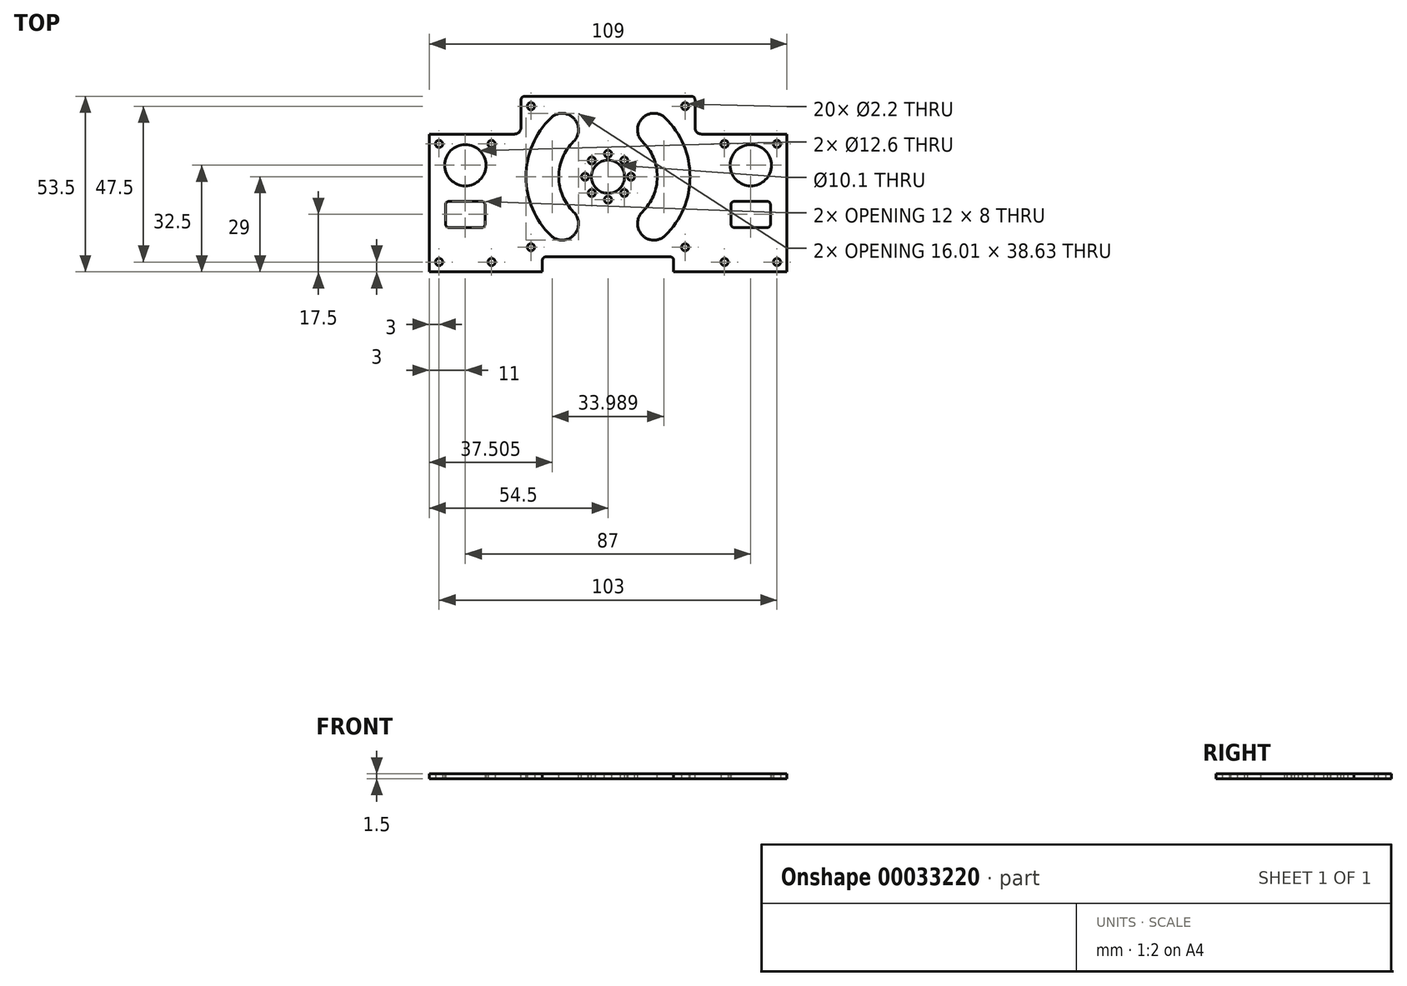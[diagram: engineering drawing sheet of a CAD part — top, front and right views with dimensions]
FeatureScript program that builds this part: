
annotation { "Feature Type Name" : "Feature", "Feature Type Description" : "" }
export const myFeature = defineFeature(function(context is Context, id is Id, definition is map)
    precondition{}
    {
        {
            var Q0;
            Q0=qCreatedBy(makeId("Top.planeOp"),FACE);
            var sketch = newSketch(context, id + "F0", { "sketchPlane" : qUnion([Q0])});
            skLineSegment(sketch, "E0.bottom", {"start": v(-54.5, 35) * mm, "end": v(54.5, 35) * mm});
            skLineSegment(sketch, "E0.top", {"start": v(-54.5, -35) * mm, "end": v(54.5, -35) * mm});
            skLineSegment(sketch, "E0.left", {"start": v(-54.5, 35) * mm, "end": v(-54.5, -35) * mm});
            skLineSegment(sketch, "E0.right", {"start": v(54.5, 35) * mm, "end": v(54.5, -35) * mm});
            skPoint(sketch, "E0.middle", {"position": v(0, 0) * mm});
            skLineSegment(sketch, "E1", {"start": v(-43.5, 35) * mm, "end": v(-43.5, -35) * mm, "construction": true});
            skCircle(sketch, "E2", {"center": v(-51.5, 10) * mm, "radius": 1.1 * mm});
            skCircle(sketch, "E3", {"center": v(-51.5, -26) * mm, "radius": 1.1 * mm});
            skCircle(sketch, "E4.MirrorC", {"center": v(-35.5, 10) * mm, "radius": 1.1 * mm});
            skCircle(sketch, "E5.MirrorC", {"center": v(-35.5, -26) * mm, "radius": 1.1 * mm});
            skCircle(sketch, "E6", {"center": v(-43.5, 3.5) * mm, "radius": 6.3 * mm});
            skCircle(sketch, "E7.MirrorC", {"center": v(35.5, -26) * mm, "radius": 1.1 * mm});
            skCircle(sketch, "E8.MirrorC", {"center": v(43.5, 3.5) * mm, "radius": 6.3 * mm});
            skCircle(sketch, "E9.MirrorC", {"center": v(35.5, 10) * mm, "radius": 1.1 * mm});
            skCircle(sketch, "E10.MirrorC", {"center": v(51.5, 10) * mm, "radius": 1.1 * mm});
            skCircle(sketch, "E11.MirrorC", {"center": v(51.5, -26) * mm, "radius": 1.1 * mm});
            skLineSegment(sketch, "E12.bottom", {"start": v(-38.5, -15.5) * mm, "end": v(-48.5, -15.5) * mm});
            skLineSegment(sketch, "E12.top", {"start": v(-38.5, -7.5) * mm, "end": v(-48.5, -7.5) * mm});
            skLineSegment(sketch, "E12.left", {"start": v(-37.5, -14.5) * mm, "end": v(-37.5, -8.5) * mm});
            skLineSegment(sketch, "E12.right", {"start": v(-49.5, -14.5) * mm, "end": v(-49.5, -8.5) * mm});
            skPoint(sketch, "E12.middle", {"position": v(-43.5, -11.5) * mm});
            skPoint(sketch, "E13.visualSharp", {"position": v(-49.5, -7.5) * mm});
            skArc(sketch, "E13.filletArc", {"start": v(-48.5, -7.5) * mm, "mid": v(-49.2, -7.8) * mm, "end": v(-49.5, -8.5) * mm});
            skPoint(sketch, "E14.visualSharp", {"position": v(-49.5, -15.5) * mm});
            skArc(sketch, "E14.filletArc", {"start": v(-49.5, -14.5) * mm, "mid": v(-49.2, -15.2) * mm, "end": v(-48.5, -15.5) * mm});
            skPoint(sketch, "E15.visualSharp", {"position": v(-37.5, -15.5) * mm});
            skArc(sketch, "E15.filletArc", {"start": v(-38.5, -15.5) * mm, "mid": v(-37.8, -15.2) * mm, "end": v(-37.5, -14.5) * mm});
            skPoint(sketch, "E16.visualSharp", {"position": v(-37.5, -7.5) * mm});
            skArc(sketch, "E16.filletArc", {"start": v(-37.5, -8.5) * mm, "mid": v(-37.8, -7.8) * mm, "end": v(-38.5, -7.5) * mm});
            skArc(sketch, "E17.MirrorCS", {"start": v(48.5, -7.5) * mm, "mid": v(49.2, -7.8) * mm, "end": v(49.5, -8.5) * mm});
            skArc(sketch, "E18.MirrorCS", {"start": v(38.5, -15.5) * mm, "mid": v(37.8, -15.2) * mm, "end": v(37.5, -14.5) * mm});
            skArc(sketch, "E19.MirrorCS", {"start": v(37.5, -8.5) * mm, "mid": v(37.8, -7.8) * mm, "end": v(38.5, -7.5) * mm});
            skArc(sketch, "E20.MirrorCS", {"start": v(49.5, -14.5) * mm, "mid": v(49.2, -15.2) * mm, "end": v(48.5, -15.5) * mm});
            skLineSegment(sketch, "E21.MirrorCS", {"start": v(49.5, -14.5) * mm, "end": v(49.5, -8.5) * mm});
            skLineSegment(sketch, "E22.MirrorCS", {"start": v(38.5, -15.5) * mm, "end": v(48.5, -15.5) * mm});
            skPoint(sketch, "E23.MirrorP", {"position": v(37.5, -15.5) * mm});
            skPoint(sketch, "E24.MirrorP", {"position": v(49.5, -15.5) * mm});
            skPoint(sketch, "E25.MirrorP", {"position": v(49.5, -7.5) * mm});
            skPoint(sketch, "E26.MirrorP", {"position": v(43.5, -11.5) * mm});
            skLineSegment(sketch, "E27.MirrorCS", {"start": v(38.5, -7.5) * mm, "end": v(48.5, -7.5) * mm});
            skLineSegment(sketch, "E28.MirrorCS", {"start": v(37.5, -14.5) * mm, "end": v(37.5, -8.5) * mm});
            skPoint(sketch, "E29.MirrorP", {"position": v(37.5, -7.5) * mm});
            skLineSegment(sketch, "E30", {"start": v(-32.5, 35) * mm, "end": v(-32.5, -35) * mm, "construction": true});
            skArc(sketch, "E31.MirrorCS", {"start": v(-27.5, -8.5) * mm, "mid": v(-27.2, -7.8) * mm, "end": v(-26.5, -7.5) * mm, "construction": true});
            skArc(sketch, "E32.MirrorCS", {"start": v(-15.5, -14.5) * mm, "mid": v(-15.8, -15.2) * mm, "end": v(-16.5, -15.5) * mm, "construction": true});
            skArc(sketch, "E33.MirrorCS", {"start": v(-26.5, -15.5) * mm, "mid": v(-27.2, -15.2) * mm, "end": v(-27.5, -14.5) * mm, "construction": true});
            skArc(sketch, "E34.MirrorCS", {"start": v(-16.5, -7.5) * mm, "mid": v(-15.8, -7.8) * mm, "end": v(-15.5, -8.5) * mm, "construction": true});
            skCircle(sketch, "E35.MirrorC", {"center": v(-13.5, -26) * mm, "radius": 1.1 * mm, "construction": true});
            skCircle(sketch, "E36.MirrorC", {"center": v(-29.5, 10) * mm, "radius": 1.1 * mm, "construction": true});
            skCircle(sketch, "E37.MirrorC", {"center": v(-29.5, -26) * mm, "radius": 1.1 * mm, "construction": true});
            skLineSegment(sketch, "E38.MirrorCS", {"start": v(-15.5, -14.5) * mm, "end": v(-15.5, -8.5) * mm, "construction": true});
            skCircle(sketch, "E39.MirrorC", {"center": v(-21.5, 3.5) * mm, "radius": 6.3 * mm, "construction": true});
            skLineSegment(sketch, "E40.MirrorCS", {"start": v(-26.5, -7.5) * mm, "end": v(-16.5, -7.5) * mm, "construction": true});
            skPoint(sketch, "E41.MirrorP", {"position": v(-21.5, -11.5) * mm});
            skLineSegment(sketch, "E42.MirrorCS", {"start": v(-27.5, -14.5) * mm, "end": v(-27.5, -8.5) * mm, "construction": true});
            skPoint(sketch, "E43.MirrorP", {"position": v(-15.5, -15.5) * mm});
            skPoint(sketch, "E44.MirrorP", {"position": v(-15.5, -7.5) * mm});
            skLineSegment(sketch, "E45.MirrorCS", {"start": v(-26.5, -15.5) * mm, "end": v(-16.5, -15.5) * mm, "construction": true});
            skPoint(sketch, "E46.MirrorP", {"position": v(-27.5, -15.5) * mm});
            skPoint(sketch, "E47.MirrorP", {"position": v(-27.5, -7.5) * mm});
            skCircle(sketch, "E48.MirrorC", {"center": v(-13.5, 10) * mm, "radius": 1.1 * mm, "construction": true});
            skArc(sketch, "E49.MirrorCS", {"start": v(15.5, -14.5) * mm, "mid": v(15.8, -15.2) * mm, "end": v(16.5, -15.5) * mm, "construction": true});
            skArc(sketch, "E50.MirrorCS", {"start": v(26.5, -15.5) * mm, "mid": v(27.2, -15.2) * mm, "end": v(27.5, -14.5) * mm, "construction": true});
            skArc(sketch, "E51.MirrorCS", {"start": v(16.5, -7.5) * mm, "mid": v(15.8, -7.8) * mm, "end": v(15.5, -8.5) * mm, "construction": true});
            skArc(sketch, "E52.MirrorCS", {"start": v(27.5, -8.5) * mm, "mid": v(27.2, -7.8) * mm, "end": v(26.5, -7.5) * mm, "construction": true});
            skLineSegment(sketch, "E53.MirrorCS", {"start": v(15.5, -14.5) * mm, "end": v(15.5, -8.5) * mm, "construction": true});
            skLineSegment(sketch, "E54.MirrorCS", {"start": v(26.5, -15.5) * mm, "end": v(16.5, -15.5) * mm, "construction": true});
            skLineSegment(sketch, "E55.MirrorCS", {"start": v(27.5, -14.5) * mm, "end": v(27.5, -8.5) * mm, "construction": true});
            skPoint(sketch, "E56.MirrorP", {"position": v(15.5, -15.5) * mm});
            skPoint(sketch, "E57.MirrorP", {"position": v(15.5, -7.5) * mm});
            skCircle(sketch, "E58.MirrorC", {"center": v(13.5, -26) * mm, "radius": 1.1 * mm, "construction": true});
            skPoint(sketch, "E59.MirrorP", {"position": v(27.5, -7.5) * mm});
            skCircle(sketch, "E60.MirrorC", {"center": v(13.5, 10) * mm, "radius": 1.1 * mm, "construction": true});
            skLineSegment(sketch, "E61.MirrorCS", {"start": v(26.5, -7.5) * mm, "end": v(16.5, -7.5) * mm, "construction": true});
            skPoint(sketch, "E62.MirrorP", {"position": v(27.5, -15.5) * mm});
            skPoint(sketch, "E63.MirrorP", {"position": v(21.5, -11.5) * mm});
            skCircle(sketch, "E64.MirrorC", {"center": v(21.5, 3.5) * mm, "radius": 6.3 * mm, "construction": true});
            skCircle(sketch, "E65.MirrorC", {"center": v(29.5, 10) * mm, "radius": 1.1 * mm, "construction": true});
            skCircle(sketch, "E66", {"center": v(-23.5, 21.5) * mm, "radius": 1.1 * mm});
            skCircle(sketch, "E67.MirrorC", {"center": v(23.5, 21.5) * mm, "radius": 1.1 * mm});
            skCircle(sketch, "E68.MirrorC", {"center": v(-23.5, -21.5) * mm, "radius": 1.1 * mm});
            skCircle(sketch, "E69.MirrorC", {"center": v(23.5, -21.5) * mm, "radius": 1.1 * mm});
            skSolve(sketch);
        }
        {
            var Q0;
            Q0=qSketchRegion(id+"F0",true);
            extrude(context, id + "F1", {"entities" : qUnion([Q0]), "depth" : 1.5 * mm});
        }
        {
            var Q0;
            Q0=makeQuery(id+"F1.opExtrude","CAP_FACE",FACE,{"disambiguationData":[OSD([sQuery(id+"F0.wireOp",EDGE,"E0.bottom"),sQuery(id+"F0.wireOp",EDGE,"E0.top"),sQuery(id+"F0.wireOp",EDGE,"E0.left"),sQuery(id+"F0.wireOp",EDGE,"E0.right"),sQuery(id+"F0.wireOp",EDGE,"E2"),sQuery(id+"F0.wireOp",EDGE,"E3"),sQuery(id+"F0.wireOp",EDGE,"E4.MirrorC"),sQuery(id+"F0.wireOp",EDGE,"E5.MirrorC"),sQuery(id+"F0.wireOp",EDGE,"E6"),sQuery(id+"F0.wireOp",EDGE,"E7.MirrorC"),sQuery(id+"F0.wireOp",EDGE,"E8.MirrorC"),sQuery(id+"F0.wireOp",EDGE,"E9.MirrorC"),sQuery(id+"F0.wireOp",EDGE,"E10.MirrorC"),sQuery(id+"F0.wireOp",EDGE,"E11.MirrorC"),sQuery(id+"F0.wireOp",EDGE,"E12.bottom"),sQuery(id+"F0.wireOp",EDGE,"E12.top"),sQuery(id+"F0.wireOp",EDGE,"E12.left"),sQuery(id+"F0.wireOp",EDGE,"E12.right"),sQuery(id+"F0.wireOp",EDGE,"E13.filletArc"),sQuery(id+"F0.wireOp",EDGE,"E14.filletArc"),sQuery(id+"F0.wireOp",EDGE,"E15.filletArc"),sQuery(id+"F0.wireOp",EDGE,"E16.filletArc"),sQuery(id+"F0.wireOp",EDGE,"E17.MirrorCS"),sQuery(id+"F0.wireOp",EDGE,"E18.MirrorCS"),sQuery(id+"F0.wireOp",EDGE,"E19.MirrorCS"),sQuery(id+"F0.wireOp",EDGE,"E20.MirrorCS"),sQuery(id+"F0.wireOp",EDGE,"E21.MirrorCS"),sQuery(id+"F0.wireOp",EDGE,"E22.MirrorCS"),sQuery(id+"F0.wireOp",EDGE,"E27.MirrorCS"),sQuery(id+"F0.wireOp",EDGE,"E28.MirrorCS"),sQuery(id+"F0.wireOp",EDGE,"E66"),sQuery(id+"F0.wireOp",EDGE,"E67.MirrorC"),sQuery(id+"F0.wireOp",EDGE,"E68.MirrorC"),sQuery(id+"F0.wireOp",EDGE,"E69.MirrorC")])],"isStart":false});
            var sketch = newSketch(context, id + "F2", { "sketchPlane" : qUnion([Q0])});
            skCircle(sketch, "E70", {"center": v(0, 0) * mm, "radius": 5.05 * mm});
            skCircle(sketch, "E71", {"center": v(0, 7) * mm, "radius": 1.1 * mm});
            skCircle(sketch, "E72.1.0", {"center": v(-4.95, 4.95) * mm, "radius": 1.1 * mm});
            skCircle(sketch, "E72.2.0", {"center": v(-7, 0) * mm, "radius": 1.1 * mm});
            skCircle(sketch, "E72.3.0", {"center": v(-4.95, -4.95) * mm, "radius": 1.1 * mm});
            skCircle(sketch, "E72.4.0", {"center": v(0, -7) * mm, "radius": 1.1 * mm});
            skCircle(sketch, "E72.5.0", {"center": v(4.95, -4.95) * mm, "radius": 1.1 * mm});
            skCircle(sketch, "E72.6.0", {"center": v(7, 0) * mm, "radius": 1.1 * mm});
            skCircle(sketch, "E72.7.0", {"center": v(4.95, 4.95) * mm, "radius": 1.1 * mm});
            skArc(sketch, "E73", {"start": v(-17.4, 17.95) * mm, "mid": v(-25, 0) * mm, "end": v(-17.4, -17.95) * mm});
            skArc(sketch, "E74", {"start": v(-10.47, 10.74) * mm, "mid": v(-15, 0) * mm, "end": v(-10.47, -10.74) * mm});
            skLineSegment(sketch, "E75", {"start": v(-9.75, 16.88) * mm, "end": v(-9.64, 16.7) * mm});
            skLineSegment(sketch, "E76.MirrorCS", {"start": v(-9.75, -16.88) * mm, "end": v(-9.64, -16.7) * mm});
            skLineSegment(sketch, "E77.MirrorCS", {"start": v(9.75, 16.88) * mm, "end": v(9.64, 16.7) * mm});
            skLineSegment(sketch, "E78.MirrorCS", {"start": v(9.75, -16.88) * mm, "end": v(9.64, -16.7) * mm});
            skArc(sketch, "E79.trimOffspring", {"start": v(10.47, -10.74) * mm, "mid": v(15, 0) * mm, "end": v(10.47, 10.74) * mm});
            skArc(sketch, "E80.trimOffspring", {"start": v(17.4, -17.95) * mm, "mid": v(25, 0) * mm, "end": v(17.4, 17.95) * mm});
            skPoint(sketch, "E81.visualSharp", {"position": v(-12.5, 21.65) * mm});
            skArc(sketch, "E81.filletArc", {"start": v(-9.75, 16.88) * mm, "mid": v(-13.31, 19.28) * mm, "end": v(-17.4, 17.95) * mm});
            skPoint(sketch, "E82.visualSharp", {"position": v(-7.5, 13) * mm});
            skArc(sketch, "E82.filletArc", {"start": v(-10.47, 10.74) * mm, "mid": v(-9.03, 13.58) * mm, "end": v(-9.64, 16.7) * mm});
            skPoint(sketch, "E83.visualSharp", {"position": v(-7.5, -13) * mm});
            skArc(sketch, "E83.filletArc", {"start": v(-9.64, -16.7) * mm, "mid": v(-9.03, -13.58) * mm, "end": v(-10.47, -10.74) * mm});
            skPoint(sketch, "E84.visualSharp", {"position": v(-12.5, -21.65) * mm});
            skArc(sketch, "E84.filletArc", {"start": v(-17.4, -17.95) * mm, "mid": v(-13.31, -19.28) * mm, "end": v(-9.75, -16.88) * mm});
            skPoint(sketch, "E85.visualSharp", {"position": v(7.5, -13) * mm});
            skArc(sketch, "E85.filletArc", {"start": v(10.47, -10.74) * mm, "mid": v(9.03, -13.58) * mm, "end": v(9.64, -16.7) * mm});
            skPoint(sketch, "E86.visualSharp", {"position": v(12.5, -21.65) * mm});
            skArc(sketch, "E86.filletArc", {"start": v(9.75, -16.88) * mm, "mid": v(13.31, -19.28) * mm, "end": v(17.4, -17.95) * mm});
            skPoint(sketch, "E87.visualSharp", {"position": v(7.5, 13) * mm});
            skArc(sketch, "E87.filletArc", {"start": v(9.64, 16.7) * mm, "mid": v(9.03, 13.58) * mm, "end": v(10.47, 10.74) * mm});
            skPoint(sketch, "E88.visualSharp", {"position": v(12.5, 21.65) * mm});
            skArc(sketch, "E88.filletArc", {"start": v(17.4, 17.95) * mm, "mid": v(13.31, 19.28) * mm, "end": v(9.75, 16.88) * mm});
            skLineSegment(sketch, "E89.bottom", {"start": v(-54.5, 35) * mm, "end": v(-26.5, 35) * mm});
            skLineSegment(sketch, "E89.top", {"start": v(-54.5, 13) * mm, "end": v(-28.5, 13) * mm});
            skLineSegment(sketch, "E89.left", {"start": v(-54.5, 35) * mm, "end": v(-54.5, 13) * mm});
            skLineSegment(sketch, "E89.right", {"start": v(-26.5, 35) * mm, "end": v(-26.5, 15) * mm});
            skPoint(sketch, "E90", {"position": v(-23.5, 21.5) * mm});
            skPoint(sketch, "E91", {"position": v(-35.5, 10) * mm});
            skLineSegment(sketch, "E92.MirrorCS", {"start": v(54.5, 13) * mm, "end": v(28.5, 13) * mm});
            skLineSegment(sketch, "E93.MirrorCS", {"start": v(54.5, 35) * mm, "end": v(26.5, 35) * mm});
            skPoint(sketch, "E94.MirrorP", {"position": v(23.5, 21.5) * mm});
            skLineSegment(sketch, "E95.MirrorCS", {"start": v(26.5, 35) * mm, "end": v(26.5, 15) * mm});
            skLineSegment(sketch, "E96.MirrorCS", {"start": v(54.5, 35) * mm, "end": v(54.5, 13) * mm});
            skPoint(sketch, "E97.MirrorP", {"position": v(35.5, 10) * mm});
            skPoint(sketch, "E98.visualSharp", {"position": v(-26.5, 13) * mm});
            skArc(sketch, "E98.filletArc", {"start": v(-28.5, 13) * mm, "mid": v(-27.09, 13.59) * mm, "end": v(-26.5, 15) * mm});
            skPoint(sketch, "E99.visualSharp", {"position": v(26.5, 13) * mm});
            skArc(sketch, "E99.filletArc", {"start": v(26.5, 15) * mm, "mid": v(27.09, 13.59) * mm, "end": v(28.5, 13) * mm});
            skLineSegment(sketch, "E100.bottom", {"start": v(-26.5, 35) * mm, "end": v(26.5, 35) * mm});
            skLineSegment(sketch, "E100.top", {"start": v(-26.5, 24.5) * mm, "end": v(26.5, 24.5) * mm});
            skLineSegment(sketch, "E100.left", {"start": v(-26.5, 35) * mm, "end": v(-26.5, 24.5) * mm});
            skLineSegment(sketch, "E100.right", {"start": v(26.5, 35) * mm, "end": v(26.5, 24.5) * mm});
            skLineSegment(sketch, "E101.bottom", {"start": v(20, -35) * mm, "end": v(-20, -35) * mm});
            skLineSegment(sketch, "E101.top", {"start": v(20, -24.43) * mm, "end": v(-20, -24.43) * mm});
            skLineSegment(sketch, "E101.left", {"start": v(20, -35) * mm, "end": v(20, -24.43) * mm});
            skLineSegment(sketch, "E101.right", {"start": v(-20, -35) * mm, "end": v(-20, -24.43) * mm});
            skPoint(sketch, "E101.middle", {"position": v(0, -29.72) * mm});
            skSolve(sketch);
        }
        {
            var Q0;
            Q0=qSketchRegion(id+"F2",true);
            extrude(context, id + "F3", {"entities" : qUnion([Q0]), "operationType" : NewBodyOperationType.REMOVE, "endBound" : BoundingType.UP_TO_NEXT, "oppositeDirection" : true, "depth" : 25 * mm});
        }
        {
            var Q0;
            Q0=makeQuery(id+"F1.opExtrude","CAP_FACE",FACE,{"disambiguationData":[OSD([sQuery(id+"F0.wireOp",EDGE,"E0.bottom"),sQuery(id+"F0.wireOp",EDGE,"E0.top"),sQuery(id+"F0.wireOp",EDGE,"E0.left"),sQuery(id+"F0.wireOp",EDGE,"E0.right"),sQuery(id+"F0.wireOp",EDGE,"E2"),sQuery(id+"F0.wireOp",EDGE,"E3"),sQuery(id+"F0.wireOp",EDGE,"E4.MirrorC"),sQuery(id+"F0.wireOp",EDGE,"E5.MirrorC"),sQuery(id+"F0.wireOp",EDGE,"E6"),sQuery(id+"F0.wireOp",EDGE,"E7.MirrorC"),sQuery(id+"F0.wireOp",EDGE,"E8.MirrorC"),sQuery(id+"F0.wireOp",EDGE,"E9.MirrorC"),sQuery(id+"F0.wireOp",EDGE,"E10.MirrorC"),sQuery(id+"F0.wireOp",EDGE,"E11.MirrorC"),sQuery(id+"F0.wireOp",EDGE,"E12.bottom"),sQuery(id+"F0.wireOp",EDGE,"E12.top"),sQuery(id+"F0.wireOp",EDGE,"E12.left"),sQuery(id+"F0.wireOp",EDGE,"E12.right"),sQuery(id+"F0.wireOp",EDGE,"E13.filletArc"),sQuery(id+"F0.wireOp",EDGE,"E14.filletArc"),sQuery(id+"F0.wireOp",EDGE,"E15.filletArc"),sQuery(id+"F0.wireOp",EDGE,"E16.filletArc"),sQuery(id+"F0.wireOp",EDGE,"E17.MirrorCS"),sQuery(id+"F0.wireOp",EDGE,"E18.MirrorCS"),sQuery(id+"F0.wireOp",EDGE,"E19.MirrorCS"),sQuery(id+"F0.wireOp",EDGE,"E20.MirrorCS"),sQuery(id+"F0.wireOp",EDGE,"E21.MirrorCS"),sQuery(id+"F0.wireOp",EDGE,"E22.MirrorCS"),sQuery(id+"F0.wireOp",EDGE,"E27.MirrorCS"),sQuery(id+"F0.wireOp",EDGE,"E28.MirrorCS"),sQuery(id+"F0.wireOp",EDGE,"E66"),sQuery(id+"F0.wireOp",EDGE,"E67.MirrorC"),sQuery(id+"F0.wireOp",EDGE,"E68.MirrorC"),sQuery(id+"F0.wireOp",EDGE,"E69.MirrorC")])],"isStart":false});
            var sketch = newSketch(context, id + "F4", { "sketchPlane" : qUnion([Q0])});
            skLineSegment(sketch, "E102.bottom", {"start": v(-54.5, -35) * mm, "end": v(-20, -35) * mm});
            skLineSegment(sketch, "E102.top", {"start": v(-54.5, -29) * mm, "end": v(-20, -29) * mm});
            skLineSegment(sketch, "E102.left", {"start": v(-54.5, -35) * mm, "end": v(-54.5, -29) * mm});
            skLineSegment(sketch, "E102.right", {"start": v(-20, -35) * mm, "end": v(-20, -29) * mm});
            skPoint(sketch, "E103", {"position": v(-51.5, -26) * mm});
            skLineSegment(sketch, "E104.MirrorCS", {"start": v(54.5, -35) * mm, "end": v(20, -35) * mm});
            skLineSegment(sketch, "E105.MirrorCS", {"start": v(54.5, -29) * mm, "end": v(20, -29) * mm});
            skLineSegment(sketch, "E106.MirrorCS", {"start": v(54.5, -35) * mm, "end": v(54.5, -29) * mm});
            skLineSegment(sketch, "E107.MirrorCS", {"start": v(20, -35) * mm, "end": v(20, -29) * mm});
            skSolve(sketch);
        }
        {
            var Q0;
            Q0 = qSketchRegion(id + "F4", true);
            extrude(context, id + "F5", {"entities" : qUnion([Q0]), "operationType" : NewBodyOperationType.REMOVE, "endBound" : BoundingType.UP_TO_NEXT, "oppositeDirection" : true, "depth" : 25 * mm});
        }
        {
            var Q0;
            Q0=makeQuery(id+"F5.boolean.opBoolean","COPY",EDGE,{"derivedFrom":makeQuery(id+"F5.opExtrude","SWEPT_EDGE",EDGE,{"disambiguationData":[OSD([sQuery(id+"F0.wireOp",EDGE,"E0.left"),sQuery(id+"F4.wireOp",EDGE,"E102.top"),sQuery(id+"F4.wireOp",EDGE,"E102.left")])]})});
            var Q1;
            Q1=makeQuery(id+"F5.boolean.opBoolean","COPY",EDGE,{"derivedFrom":makeQuery(id+"F5.opExtrude","SWEPT_EDGE",EDGE,{"disambiguationData":[OSD([sQuery(id+"F2.wireOp",EDGE,"E101.right"),sQuery(id+"F4.wireOp",EDGE,"E102.top"),sQuery(id+"F4.wireOp",EDGE,"E102.right")])]})});
            var Q2;
            Q2=makeQuery(id+"F5.boolean.opBoolean","COPY",EDGE,{"derivedFrom":makeQuery(id+"F5.opExtrude","SWEPT_EDGE",EDGE,{"disambiguationData":[OSD([sQuery(id+"F2.wireOp",EDGE,"E101.left"),sQuery(id+"F4.wireOp",EDGE,"E105.MirrorCS"),sQuery(id+"F4.wireOp",EDGE,"E107.MirrorCS")])]})});
            var Q3;
            Q3=makeQuery(id+"F5.boolean.opBoolean","COPY",EDGE,{"derivedFrom":makeQuery(id+"F5.opExtrude","SWEPT_EDGE",EDGE,{"disambiguationData":[OSD([sQuery(id+"F0.wireOp",EDGE,"E0.right"),sQuery(id+"F4.wireOp",EDGE,"E105.MirrorCS"),sQuery(id+"F4.wireOp",EDGE,"E106.MirrorCS")])]})});
            var Q4;
            Q4=makeQuery(id+"F3.boolean.opBoolean","COPY",EDGE,{"derivedFrom":makeQuery(id+"F3.opExtrude","SWEPT_EDGE",EDGE,{"disambiguationData":[OSD([sQuery(id+"F2.wireOp",EDGE,"E101.top"),sQuery(id+"F2.wireOp",EDGE,"E101.right")])]})});
            var Q5;
            Q5=makeQuery(id+"F3.boolean.opBoolean","COPY",EDGE,{"derivedFrom":makeQuery(id+"F3.opExtrude","SWEPT_EDGE",EDGE,{"disambiguationData":[OSD([sQuery(id+"F2.wireOp",EDGE,"E101.top"),sQuery(id+"F2.wireOp",EDGE,"E101.left")])]})});
            var Q6;
            Q6=makeQuery(id+"F3.boolean.opBoolean","COPY",EDGE,{"derivedFrom":makeQuery(id+"F3.opExtrude","SWEPT_EDGE",EDGE,{"disambiguationData":[OSD([sQuery(id+"F0.wireOp",EDGE,"E0.right"),sQuery(id+"F2.wireOp",EDGE,"E92.MirrorCS"),sQuery(id+"F2.wireOp",EDGE,"E96.MirrorCS")])]})});
            var Q7;
            Q7=makeQuery(id+"F3.boolean.opBoolean","COPY",EDGE,{"derivedFrom":makeQuery(id+"F3.opExtrude","SWEPT_EDGE",EDGE,{"disambiguationData":[OSD([sQuery(id+"F2.wireOp",EDGE,"E95.MirrorCS"),sQuery(id+"F2.wireOp",EDGE,"E100.top"),sQuery(id+"F2.wireOp",EDGE,"E100.right")])]})});
            var Q8;
            Q8=makeQuery(id+"F3.boolean.opBoolean","COPY",EDGE,{"derivedFrom":makeQuery(id+"F3.opExtrude","SWEPT_EDGE",EDGE,{"disambiguationData":[OSD([sQuery(id+"F2.wireOp",EDGE,"E89.right"),sQuery(id+"F2.wireOp",EDGE,"E100.top"),sQuery(id+"F2.wireOp",EDGE,"E100.left")])]})});
            var Q9;
            Q9=makeQuery(id+"F3.boolean.opBoolean","COPY",EDGE,{"derivedFrom":makeQuery(id+"F3.opExtrude","SWEPT_EDGE",EDGE,{"disambiguationData":[OSD([sQuery(id+"F0.wireOp",EDGE,"E0.left"),sQuery(id+"F2.wireOp",EDGE,"E89.top"),sQuery(id+"F2.wireOp",EDGE,"E89.left")])]})});
            fillet(context, id + "F6", {"entities" : qUnion([Q0, Q1, Q2, Q3, Q4, Q5, Q6, Q7, Q8, Q9]), "radius" : 1 * mm, "tangentPropagation" : true, "allowEdgeOverflow" : false});
        }
    });
